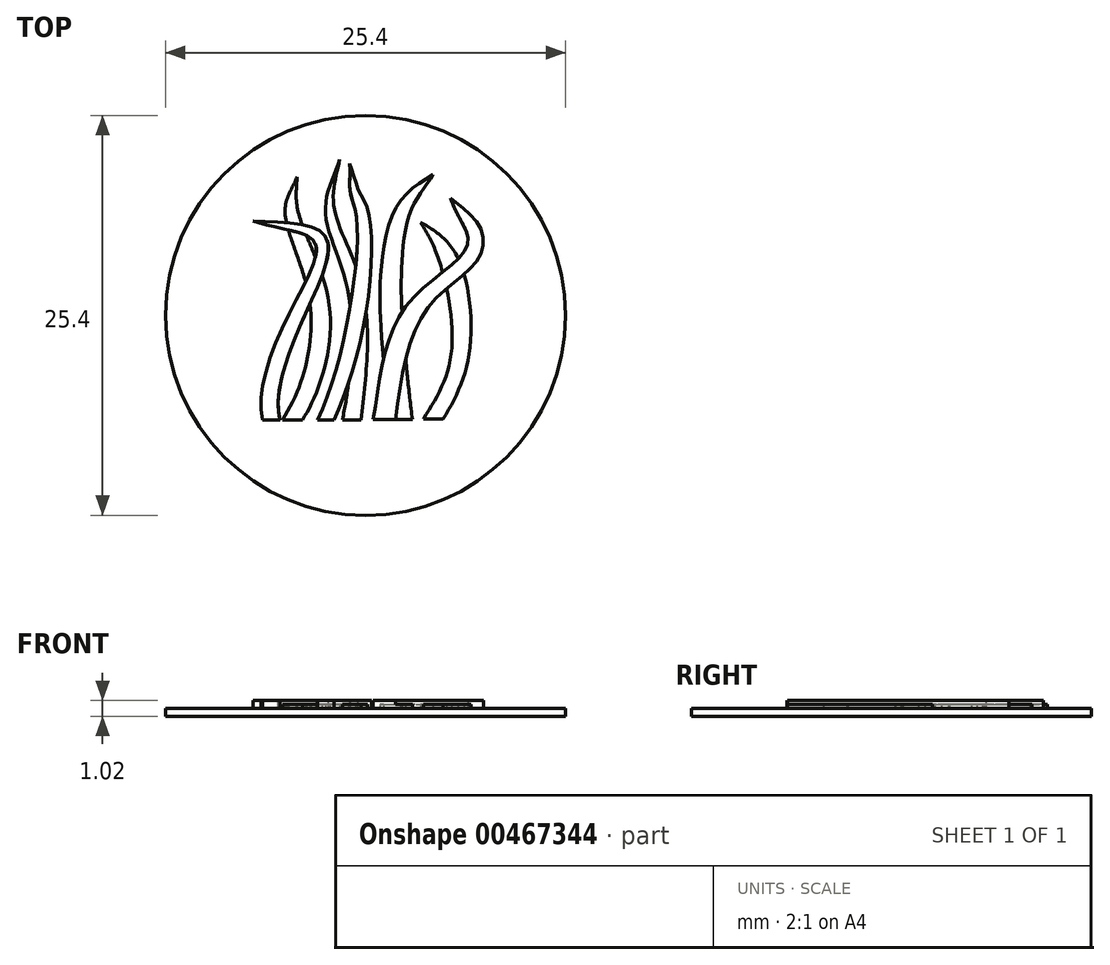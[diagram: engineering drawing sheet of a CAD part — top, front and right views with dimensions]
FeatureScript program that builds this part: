
annotation { "Feature Type Name" : "Feature", "Feature Type Description" : "" }
export const myFeature = defineFeature(function(context is Context, id is Id, definition is map)
    precondition{}
    {
        {
            var Q0;
            Q0=qCreatedBy(makeId("Top.planeOp"),FACE);
            var sketch = newSketch(context, id + "F0", { "sketchPlane" : qUnion([Q0])});
            skCircle(sketch, "E0", {"center": v(0, 0) * mm, "radius": 12.7 * mm});
            skSolve(sketch);
        }
        {
            var Q0;
            Q0=qSketchRegion(id+"F0",true);
            extrude(context, id + "F1", {"entities" : qUnion([Q0]), "depth" : 0.5 * mm});
        }
        {
            var Q0;
            {var subQ0=sQuery(id+"F0.wireOp",EDGE,"E0");Q0=makeQuery(id+"FfgjwBGc4vz0o7k_1.boolean.opBoolean","SPLIT",FACE,{"disambiguationData":[TD([makeQuery(id+"F1.opExtrude","SWEPT_FACE",FACE,{"disambiguationData":[OSD([subQ0])]})])],"derivedFrom":makeQuery(id+"F1.opExtrude","CAP_FACE",FACE,{"disambiguationData":[OSD([subQ0])],"isStart":false})});}
            var sketch = newSketch(context, id + "F2", { "sketchPlane" : qUnion([Q0])});
            skFitSpline(sketch, "E1", {"points": [v(-5.27, -6.63) * mm, v(-3.58, 1.06) * mm, v(-5.11, 6.7) * mm, v(-4.36, 8.8) * mm], "startDerivative": vector(10.04, 15.61) * mm, "endDerivative": vector(3.06, 8.63) * mm});
            skFitSpline(sketch, "E2", {"points": [v(-4.36, 8.8) * mm, v(-4.31, 6.73) * mm, v(-2.46, 1.55) * mm, v(-2.7, -3.66) * mm, v(-4, -6.63) * mm], "startDerivative": vector(-0.1, -9.72) * mm, "endDerivative": vector(-5.57, -8.38) * mm});
            skLineSegment(sketch, "E3", {"start": v(-5.27, -6.63) * mm, "end": v(-4, -6.63) * mm});
            skFitSpline(sketch, "E4", {"points": [v(-1.47, -6.63) * mm, v(-1.13, 1.58) * mm, v(-2.55, 6.7) * mm, v(-1.64, 9.9) * mm], "startDerivative": vector(3.53, 17.26) * mm, "endDerivative": vector(3.8, 11.23) * mm});
            skFitSpline(sketch, "E5", {"points": [v(-1.64, 9.9) * mm, v(-2, 6.9) * mm, v(-0.2, 1.79) * mm, v(-0.3, -6.63) * mm], "startDerivative": vector(-2.2, -10.92) * mm, "endDerivative": vector(-2.45, -17.83) * mm});
            skLineSegment(sketch, "E6", {"start": v(-1.47, -6.63) * mm, "end": v(-0.3, -6.63) * mm});
            skFitSpline(sketch, "E7", {"points": [v(1.51, -6.62) * mm, v(0.94, 0) * mm, v(0.95, 2.3) * mm, v(1.89, 6.77) * mm, v(4.3, 8.93) * mm], "startDerivative": vector(-3, 24.36) * mm, "endDerivative": vector(12.68, 7.08) * mm});
            skFitSpline(sketch, "E8", {"points": [v(4.3, 8.93) * mm, v(2.82, 6.52) * mm, v(2.27, 2.13) * mm, v(2.33, 0) * mm, v(2.97, -6.62) * mm], "startDerivative": vector(-5.95, -9.9) * mm, "endDerivative": vector(2.93, -23.32) * mm});
            skFitSpline(sketch, "E9", {"points": [v(3.68, -6.6) * mm, v(5.44, -2.43) * mm, v(4.62, 3.63) * mm, v(3.5, 5.91) * mm], "startDerivative": vector(6.79, 10.86) * mm, "endDerivative": vector(-4.39, 7.34) * mm});
            skFitSpline(sketch, "E10", {"points": [v(3.5, 5.91) * mm, v(5.76, 3.86) * mm, v(6.58, -2.46) * mm, v(4.93, -6.6) * mm], "startDerivative": vector(9.16, -5.4) * mm, "endDerivative": vector(-6.3, -11.01) * mm});
            skLineSegment(sketch, "E11", {"start": v(1.51, -6.62) * mm, "end": v(2.97, -6.62) * mm});
            skLineSegment(sketch, "E12", {"start": v(3.68, -6.6) * mm, "end": v(4.93, -6.6) * mm});
            skSolve(sketch);
        }
        {
            var Q0;
            Q0 = qSketchRegion(id + "F2", true);
            extrude(context, id + "F3", {"entities" : qUnion([Q0]), "operationType" : NewBodyOperationType.ADD, "depth" : 0.25 * mm});
        }
        {
            var Q0;
            {var subQ0=sQuery(id+"F0.wireOp",EDGE,"E0");Q0=makeQuery(id+"FfgjwBGc4vz0o7k_1.boolean.opBoolean","SPLIT",FACE,{"disambiguationData":[TD([makeQuery(id+"F1.opExtrude","SWEPT_FACE",FACE,{"disambiguationData":[OSD([subQ0])]})])],"derivedFrom":makeQuery(id+"F1.opExtrude","CAP_FACE",FACE,{"disambiguationData":[OSD([subQ0])],"isStart":false})});}
            var sketch = newSketch(context, id + "F4", { "sketchPlane" : qUnion([Q0])});
            skFitSpline(sketch, "E13", {"points": [v(-3.04, -6.63) * mm, v(-0.99, 0.5) * mm, v(-0.61, 6.45) * mm, v(-1, 7.98) * mm, v(-1.02, 9.66) * mm], "startDerivative": vector(7.19, 14.72) * mm, "endDerivative": vector(-1.46, 8.96) * mm});
            skFitSpline(sketch, "E14", {"points": [v(-1.02, 9.66) * mm, v(-0.49, 8.08) * mm, v(0.18, 6.57) * mm, v(0, 0) * mm, v(-2, -6.63) * mm], "startDerivative": vector(3.42, -7.05) * mm, "endDerivative": vector(-6.6, -13.99) * mm});
            skLineSegment(sketch, "E15", {"start": v(-3.04, -6.63) * mm, "end": v(-2, -6.63) * mm});
            skFitSpline(sketch, "E16", {"points": [v(-5.43, -6.63) * mm, v(-4.21, -0.78) * mm, v(-2.54, 5.02) * mm, v(-7.15, 6) * mm], "startDerivative": vector(-3.38, 12.92) * mm, "endDerivative": vector(-17.42, 1.26) * mm});
            skFitSpline(sketch, "E17", {"points": [v(-7.15, 6) * mm, v(-5.18, 5.48) * mm, v(-3.19, 4.57) * mm, v(-5.08, -0.34) * mm, v(-6.53, -6.63) * mm], "startDerivative": vector(10, -3) * mm, "endDerivative": vector(3.85, -13.63) * mm});
            skLineSegment(sketch, "E18", {"start": v(-6.53, -6.63) * mm, "end": v(-5.43, -6.63) * mm});
            skFitSpline(sketch, "E19", {"points": [v(0.5, -6.62) * mm, v(2.71, 0.77) * mm, v(6.5, 4.56) * mm, v(5.41, 7.46) * mm], "startDerivative": vector(3.29, 20.23) * mm, "endDerivative": vector(-3.3, 13.54) * mm});
            skFitSpline(sketch, "E20", {"points": [v(5.41, 7.46) * mm, v(7.26, 5.62) * mm, v(7.02, 3.4) * mm, v(3.92, 0.43) * mm, v(1.9, -6.62) * mm], "startDerivative": vector(6.48, -5.76) * mm, "endDerivative": vector(-2.69, -22.92) * mm});
            skLineSegment(sketch, "E21", {"start": v(0.5, -6.62) * mm, "end": v(1.9, -6.62) * mm});
            skSolve(sketch);
        }
        {
            var Q0;
            Q0 = qSketchRegion(id + "F4", true);
            extrude(context, id + "F5", {"entities" : qUnion([Q0]), "operationType" : NewBodyOperationType.ADD, "depth" : 0.5 * mm});
        }
    });
